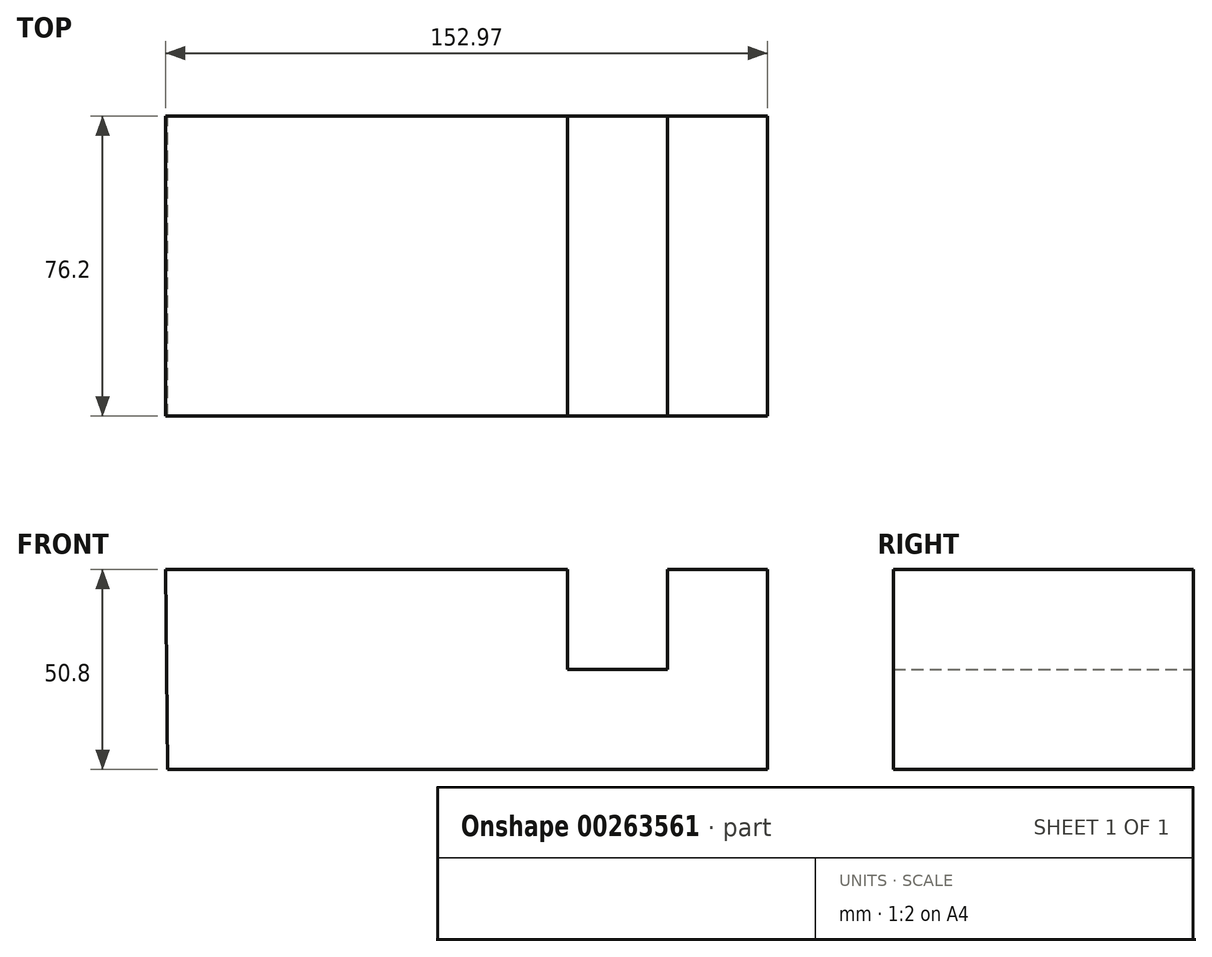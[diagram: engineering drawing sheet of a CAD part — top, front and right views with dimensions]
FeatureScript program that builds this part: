
annotation { "Feature Type Name" : "Feature", "Feature Type Description" : "" }
export const myFeature = defineFeature(function(context is Context, id is Id, definition is map)
    precondition{}
    {
        {
            var Q0;
            Q0=qCreatedBy(makeId("Front.planeOp"),FACE);
            var sketch = newSketch(context, id + "F0", { "sketchPlane" : qUnion([Q0])});
            skLineSegment(sketch, "E0", {"start": v(-76.27, -48.06) * mm, "end": v(76.13, -48.06) * mm});
            skLineSegment(sketch, "E1", {"start": v(76.13, -48.06) * mm, "end": v(76.13, 2.74) * mm});
            skLineSegment(sketch, "E2", {"start": v(76.13, 2.74) * mm, "end": v(50.73, 2.74) * mm});
            skLineSegment(sketch, "E3", {"start": v(50.73, 2.74) * mm, "end": v(50.73, -22.66) * mm});
            skLineSegment(sketch, "E4", {"start": v(50.73, -22.66) * mm, "end": v(25.33, -22.66) * mm});
            skLineSegment(sketch, "E5", {"start": v(25.33, -22.66) * mm, "end": v(25.33, 2.74) * mm});
            skLineSegment(sketch, "E6", {"start": v(25.33, 2.74) * mm, "end": v(-76.84, 2.74) * mm});
            skLineSegment(sketch, "E7", {"start": v(-76.84, 2.74) * mm, "end": v(-76.27, -48.06) * mm});
            skSolve(sketch);
        }
        {
            var Q0;
            Q0=makeQuery(id+"F0.imprint","IMPRINT",FACE,{"disambiguationData":[TD([[makeQuery(id+"F0.imprint","IMPRINT",EDGE,{"derivedFrom":sQuery(id+"F0.wireOp",EDGE,"E0")}),1.0]])]});
            extrude(context, id + "F1", {"entities" : qUnion([Q0]), "depth" : 76.2 * mm});
        }
    });
